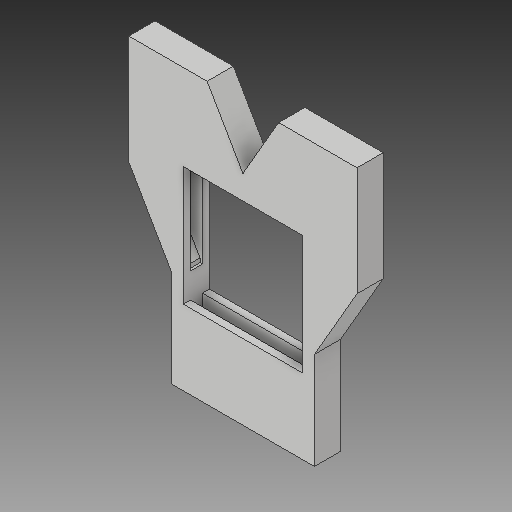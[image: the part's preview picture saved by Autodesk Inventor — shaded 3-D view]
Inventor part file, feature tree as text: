
AUTODESK INVENTOR PART (.ipt)
format: ipt  version: 2017 (Build 210142000, 142)  size: 146,944 bytes
history: native  units: in
note: dims shown in document units (in); Inventor stores cm internally (conversion verified against a paired STEP export)
features: other x4, plane x1, sketch x1
ambient origin geometry x8: Origin, YZ Plane, XZ Plane, XY Plane, X Axis, Y Axis, Z Axis, Center Point
bodies: Solid1 (feature_tree)
feature tree (6):
  other  "end door frame (100).ipt"
  plane  "Work Plane1"
  sketch  "Sketch1"  dims[d0=0.0354in d1=4.5in]
  other  "mate for doors"
  other  "rame of door::end door frame (100).ipt"
  other  "TaggingFeature1"
